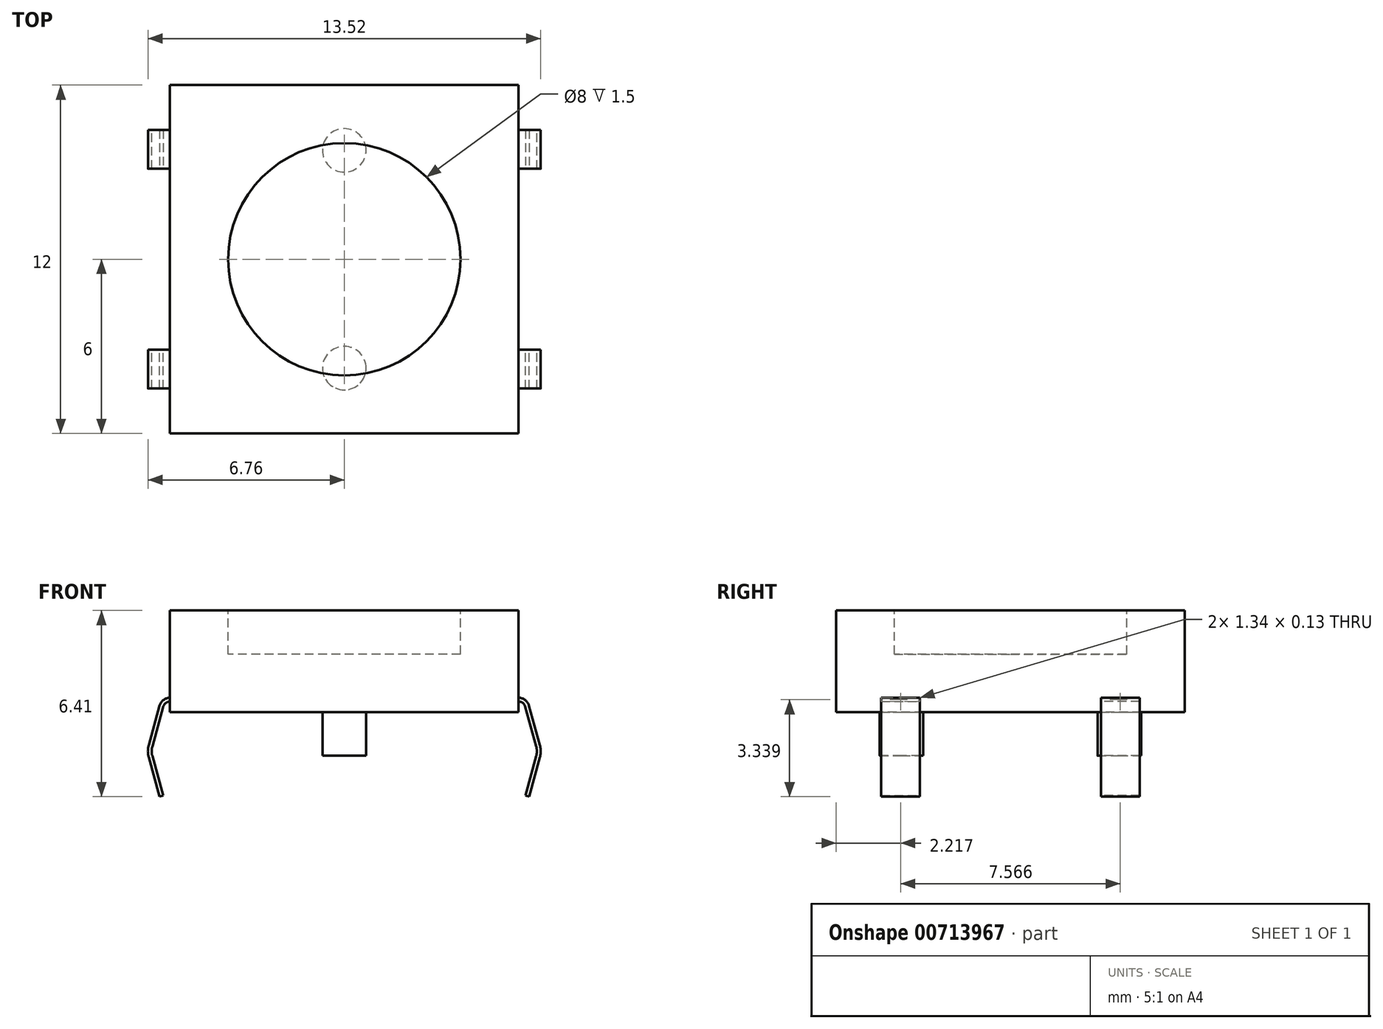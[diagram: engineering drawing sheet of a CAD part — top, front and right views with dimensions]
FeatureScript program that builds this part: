
annotation { "Feature Type Name" : "Feature", "Feature Type Description" : "" }
export const myFeature = defineFeature(function(context is Context, id is Id, definition is map)
    precondition{}
    {
        {
            var Q0;
            Q0=qCreatedBy(makeId("Top.planeOp"),FACE);
            var sketch = newSketch(context, id + "F0", { "sketchPlane" : qUnion([Q0])});
            skLineSegment(sketch, "E0.bottom", {"start": v(6, -6) * mm, "end": v(-6, -6) * mm});
            skLineSegment(sketch, "E0.top", {"start": v(6, 6) * mm, "end": v(-6, 6) * mm});
            skLineSegment(sketch, "E0.left", {"start": v(6, -6) * mm, "end": v(6, 6) * mm});
            skLineSegment(sketch, "E0.right", {"start": v(-6, -6) * mm, "end": v(-6, 6) * mm});
            skPoint(sketch, "E0.middle", {"position": v(0, 0) * mm});
            skSolve(sketch);
        }
        {
            var Q0;
            Q0 = qSketchRegion(id + "F0", true);
            extrude(context, id + "F1", {"entities" : qUnion([Q0]), "oppositeDirection" : true, "depth" : 3.5 * mm, "offsetDistance" : 25 * mm});
        }
        {
            var Q0;
            Q0=qCreatedBy(makeId("Top.planeOp"),FACE);
            var sketch = newSketch(context, id + "F2", { "sketchPlane" : qUnion([Q0])});
            skCircle(sketch, "E1", {"center": v(0, 0) * mm, "radius": 4 * mm});
            skSolve(sketch);
        }
        {
            var Q0;
            Q0 = qSketchRegion(id + "F2", true);
            extrude(context, id + "F3", {"entities" : qUnion([Q0]), "operationType" : NewBodyOperationType.REMOVE, "oppositeDirection" : true, "depth" : 1.5 * mm, "offsetDistance" : 25 * mm});
        }
        {
            var Q0;
            Q0=makeQuery(id+"F1.opExtrude","CAP_FACE",FACE,{"disambiguationData":[OSD([sQuery(id+"F0.wireOp",EDGE,"E0.bottom"),sQuery(id+"F0.wireOp",EDGE,"E0.top"),sQuery(id+"F0.wireOp",EDGE,"E0.left"),sQuery(id+"F0.wireOp",EDGE,"E0.right")])],"isStart":false});
            var sketch = newSketch(context, id + "F4", { "sketchPlane" : qUnion([Q0])});
            skCircle(sketch, "E2", {"center": v(0, -3.75) * mm, "radius": 0.75 * mm});
            skCircle(sketch, "E3.MirrorC", {"center": v(0, 3.75) * mm, "radius": 0.75 * mm});
            skSolve(sketch);
        }
        {
            var Q0;
            Q0 = qSketchRegion(id + "F4", true);
            extrude(context, id + "F5", {"entities" : qUnion([Q0]), "operationType" : NewBodyOperationType.ADD, "depth" : 1.5 * mm, "offsetDistance" : 25 * mm});
        }
        {
            var Q0;
            Q0=makeQuery(id+"F1.opExtrude","SWEPT_FACE",FACE,{"disambiguationData":[OSD([sQuery(id+"F0.wireOp",EDGE,"E0.left")])]});
            var sketch = newSketch(context, id + "F6", { "sketchPlane" : qUnion([Q0])});
            skLineSegment(sketch, "E4.bottom", {"start": v(-4.45, -3) * mm, "end": v(-3.11, -3) * mm});
            skLineSegment(sketch, "E4.top", {"start": v(-4.45, -3.14) * mm, "end": v(-3.11, -3.14) * mm});
            skLineSegment(sketch, "E4.left", {"start": v(-4.45, -3) * mm, "end": v(-4.45, -3.14) * mm});
            skLineSegment(sketch, "E4.right", {"start": v(-3.11, -3) * mm, "end": v(-3.11, -3.14) * mm});
            skLineSegment(sketch, "E5.MirrorCS", {"start": v(3.11, -3) * mm, "end": v(3.11, -3.14) * mm});
            skLineSegment(sketch, "E6.MirrorCS", {"start": v(4.45, -3) * mm, "end": v(4.45, -3.14) * mm});
            skLineSegment(sketch, "E7.MirrorCS", {"start": v(4.45, -3.14) * mm, "end": v(3.11, -3.14) * mm});
            skLineSegment(sketch, "E8.MirrorCS", {"start": v(4.45, -3) * mm, "end": v(3.11, -3) * mm});
            skSolve(sketch);
        }
        {
            var Q0;
            Q0=makeQuery(id+"F1.opExtrude","SWEPT_FACE",FACE,{"disambiguationData":[OSD([sQuery(id+"F0.wireOp",EDGE,"E0.top")])]});
            var sketch = newSketch(context, id + "F7", { "sketchPlane" : qUnion([Q0])});
            skArc(sketch, "E9", {"start": v(-6, -2.98) * mm, "mid": v(-6.24, -3.06) * mm, "end": v(-6.38, -3.27) * mm});
            skLineSegment(sketch, "E10", {"start": v(-6.38, -3.27) * mm, "end": v(-6.76, -4.64) * mm});
            skArc(sketch, "E11", {"start": v(-6.76, -4.64) * mm, "mid": v(-6.79, -4.85) * mm, "end": v(-6.76, -5.06) * mm});
            skLineSegment(sketch, "E12", {"start": v(-6.76, -5.06) * mm, "end": v(-6.38, -6.41) * mm});
            skSolve(sketch);
        }
        {
            var Q0;
            Q0 = qSketchRegion(id + "F6", true);
            var Q1;
            Q1=sQuery(id+"F7.wireOp",EDGE,"E10");
            var Q2;
            Q2=sQuery(id+"F7.wireOp",EDGE,"E9");
            var Q3;
            Q3=sQuery(id+"F7.wireOp",EDGE,"E12");
            var Q4;
            Q4=sQuery(id+"F7.wireOp",EDGE,"E11");
            sweep(context, id + "F8", {"profiles" : qUnion([Q0]), "path" : qUnion([Q1, Q2, Q3, Q4])});
        }
        {
            var Q0;
            Q0=makeQuery(id+"F8.opSweep","SWEPT_BODY",BODY,{"disambiguationData":[OSD([sQuery(id+"F6.wireOp",EDGE,"E4.bottom"),sQuery(id+"F6.wireOp",EDGE,"E4.top"),sQuery(id+"F6.wireOp",EDGE,"E4.left"),sQuery(id+"F6.wireOp",EDGE,"E4.right"),sQuery(id+"F7.wireOp",EDGE,"E9")])]});
            var Q1;
            Q1=makeQuery(id+"F8.opSweep","SWEPT_BODY",BODY,{"disambiguationData":[OSD([sQuery(id+"F6.wireOp",EDGE,"E5.MirrorCS"),sQuery(id+"F6.wireOp",EDGE,"E6.MirrorCS"),sQuery(id+"F6.wireOp",EDGE,"E7.MirrorCS"),sQuery(id+"F6.wireOp",EDGE,"E8.MirrorCS"),sQuery(id+"F7.wireOp",EDGE,"E9")])]});
            var Q2;
            Q2=qCreatedBy(makeId("Right.planeOp"),FACE);
            mirror(context, id + "F9", {"operationType" : NewBodyOperationType.ADD, "entities" : qUnion([Q0, Q1]), "mirrorPlane" : qUnion([Q2])});
        }
    });
